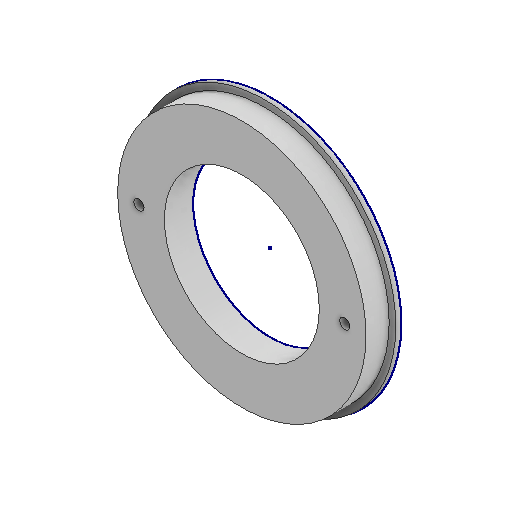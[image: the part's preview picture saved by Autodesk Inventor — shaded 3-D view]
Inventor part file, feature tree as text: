
AUTODESK INVENTOR PART (.ipt)
format: ipt  version: 2023 (Build 270158000, 158)  size: 121,344 bytes
history: native  units: mm
features: extrude x2, sketch x1, hole x1
ambient origin geometry x8: Origin, YZ Plane, XZ Plane, XY Plane, X Axis, Y Axis, Z Axis, Center Point
bodies: Solid1 (feature_tree)
feature tree (4):
  sketch  "Sketch1"  dims[d0=30.1mm d1=48.25mm d2=50.8mm d3=5.5mm d4=0.0mm d5=1.0mm d6=0.0mm d7=2.0mm d8=6.0mm d9=4.0mm d10=2.0mm d11=90.0deg d12=8.0mm d13=20.594885mm]
  extrude  "Extrusion1"  Depth=1.0mm
  extrude  "Extrusion2"  Depth=1.0mm
  hole  "Hole1"  [1 undecoded]
note: 1 required parameter value undecoded (feature->parameter linkage not recoverable at this tier; creation-order binding heuristic only, values carry confidence <= 0.55)
